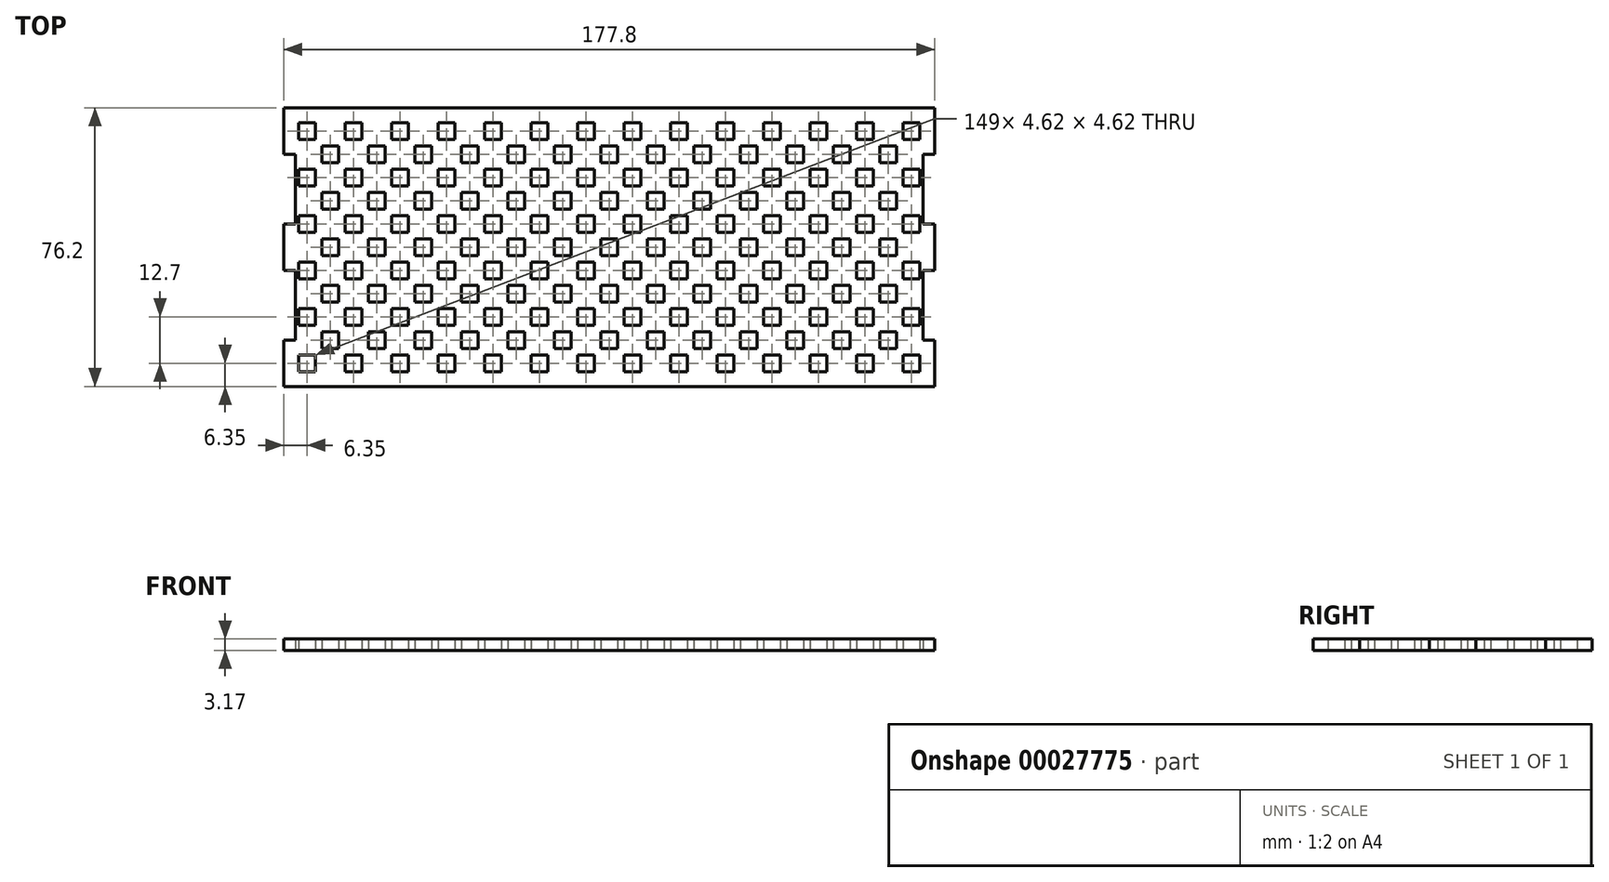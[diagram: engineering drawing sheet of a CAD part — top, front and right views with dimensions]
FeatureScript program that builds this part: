
annotation { "Feature Type Name" : "Feature", "Feature Type Description" : "" }
export const myFeature = defineFeature(function(context is Context, id is Id, definition is map)
    precondition{}
    {
        {
            var Q0;
            Q0=qCreatedBy(makeId("Top.planeOp"),FACE);
            var sketch = newSketch(context, id + "F0", { "sketchPlane" : qUnion([Q0])});
            skLineSegment(sketch, "E0.rect.bottom", {"start": v(88.9, 38.1) * mm, "end": v(-88.9, 38.1) * mm});
            skLineSegment(sketch, "E0.rect.top", {"start": v(88.9, -38.1) * mm, "end": v(-88.9, -38.1) * mm});
            skLineSegment(sketch, "E0.rect.left", {"start": v(88.9, 38.1) * mm, "end": v(88.9, 25.4) * mm});
            skLineSegment(sketch, "E0.rect.right", {"start": v(-88.9, 38.1) * mm, "end": v(-88.9, 25.4) * mm});
            skPoint(sketch, "E0.rect.middle", {"position": v(0, 0) * mm});
            skPoint(sketch, "E1", {"position": v(-88.9, 34.06) * mm});
            skPoint(sketch, "E2", {"position": v(-84.86, 34.06) * mm});
            skLineSegment(sketch, "E3.bottom", {"start": v(-84.86, 34.06) * mm, "end": v(-80.24, 34.06) * mm});
            skLineSegment(sketch, "E3.top", {"start": v(-84.86, 29.44) * mm, "end": v(-80.24, 29.44) * mm});
            skLineSegment(sketch, "E3.left", {"start": v(-84.86, 34.06) * mm, "end": v(-84.86, 29.44) * mm});
            skLineSegment(sketch, "E3.right", {"start": v(-80.24, 34.06) * mm, "end": v(-80.24, 29.44) * mm});
            skLineSegment(sketch, "E4.1.0.0", {"start": v(-72.16, 34.06) * mm, "end": v(-72.16, 29.44) * mm});
            skLineSegment(sketch, "E4.1.0.1", {"start": v(-72.16, 34.06) * mm, "end": v(-67.54, 34.06) * mm});
            skLineSegment(sketch, "E4.1.0.2", {"start": v(-67.54, 34.06) * mm, "end": v(-67.54, 29.44) * mm});
            skLineSegment(sketch, "E4.1.0.3", {"start": v(-72.16, 29.44) * mm, "end": v(-67.54, 29.44) * mm});
            skLineSegment(sketch, "E4.2.0.0", {"start": v(-59.46, 34.06) * mm, "end": v(-59.46, 29.44) * mm});
            skLineSegment(sketch, "E4.2.0.1", {"start": v(-59.46, 34.06) * mm, "end": v(-54.84, 34.06) * mm});
            skLineSegment(sketch, "E4.2.0.2", {"start": v(-54.84, 34.06) * mm, "end": v(-54.84, 29.44) * mm});
            skLineSegment(sketch, "E4.2.0.3", {"start": v(-59.46, 29.44) * mm, "end": v(-54.84, 29.44) * mm});
            skLineSegment(sketch, "E4.3.0.0", {"start": v(-46.76, 34.06) * mm, "end": v(-46.76, 29.44) * mm});
            skLineSegment(sketch, "E4.3.0.1", {"start": v(-46.76, 34.06) * mm, "end": v(-42.14, 34.06) * mm});
            skLineSegment(sketch, "E4.3.0.2", {"start": v(-42.14, 34.06) * mm, "end": v(-42.14, 29.44) * mm});
            skLineSegment(sketch, "E4.3.0.3", {"start": v(-46.76, 29.44) * mm, "end": v(-42.14, 29.44) * mm});
            skLineSegment(sketch, "E4.4.0.0", {"start": v(-34.06, 34.06) * mm, "end": v(-34.06, 29.44) * mm});
            skLineSegment(sketch, "E4.4.0.1", {"start": v(-34.06, 34.06) * mm, "end": v(-29.44, 34.06) * mm});
            skLineSegment(sketch, "E4.4.0.2", {"start": v(-29.44, 34.06) * mm, "end": v(-29.44, 29.44) * mm});
            skLineSegment(sketch, "E4.4.0.3", {"start": v(-34.06, 29.44) * mm, "end": v(-29.44, 29.44) * mm});
            skLineSegment(sketch, "E4.5.0.0", {"start": v(-21.36, 34.06) * mm, "end": v(-21.36, 29.44) * mm});
            skLineSegment(sketch, "E4.5.0.1", {"start": v(-21.36, 34.06) * mm, "end": v(-16.74, 34.06) * mm});
            skLineSegment(sketch, "E4.5.0.2", {"start": v(-16.74, 34.06) * mm, "end": v(-16.74, 29.44) * mm});
            skLineSegment(sketch, "E4.5.0.3", {"start": v(-21.36, 29.44) * mm, "end": v(-16.74, 29.44) * mm});
            skLineSegment(sketch, "E4.6.0.0", {"start": v(-8.66, 34.06) * mm, "end": v(-8.66, 29.44) * mm});
            skLineSegment(sketch, "E4.6.0.1", {"start": v(-8.66, 34.06) * mm, "end": v(-4.04, 34.06) * mm});
            skLineSegment(sketch, "E4.6.0.2", {"start": v(-4.04, 34.06) * mm, "end": v(-4.04, 29.44) * mm});
            skLineSegment(sketch, "E4.6.0.3", {"start": v(-8.66, 29.44) * mm, "end": v(-4.04, 29.44) * mm});
            skLineSegment(sketch, "E4.7.0.0", {"start": v(4.04, 34.06) * mm, "end": v(4.04, 29.44) * mm});
            skLineSegment(sketch, "E4.7.0.1", {"start": v(4.04, 34.06) * mm, "end": v(8.66, 34.06) * mm});
            skLineSegment(sketch, "E4.7.0.2", {"start": v(8.66, 34.06) * mm, "end": v(8.66, 29.44) * mm});
            skLineSegment(sketch, "E4.7.0.3", {"start": v(4.04, 29.44) * mm, "end": v(8.66, 29.44) * mm});
            skLineSegment(sketch, "E4.8.0.0", {"start": v(16.74, 34.06) * mm, "end": v(16.74, 29.44) * mm});
            skLineSegment(sketch, "E4.8.0.1", {"start": v(16.74, 34.06) * mm, "end": v(21.36, 34.06) * mm});
            skLineSegment(sketch, "E4.8.0.2", {"start": v(21.36, 34.06) * mm, "end": v(21.36, 29.44) * mm});
            skLineSegment(sketch, "E4.8.0.3", {"start": v(16.74, 29.44) * mm, "end": v(21.36, 29.44) * mm});
            skLineSegment(sketch, "E4.9.0.0", {"start": v(29.44, 34.06) * mm, "end": v(29.44, 29.44) * mm});
            skLineSegment(sketch, "E4.9.0.1", {"start": v(29.44, 34.06) * mm, "end": v(34.06, 34.06) * mm});
            skLineSegment(sketch, "E4.9.0.2", {"start": v(34.06, 34.06) * mm, "end": v(34.06, 29.44) * mm});
            skLineSegment(sketch, "E4.9.0.3", {"start": v(29.44, 29.44) * mm, "end": v(34.06, 29.44) * mm});
            skLineSegment(sketch, "E4.10.0.0", {"start": v(42.14, 34.06) * mm, "end": v(42.14, 29.44) * mm});
            skLineSegment(sketch, "E4.10.0.1", {"start": v(42.14, 34.06) * mm, "end": v(46.76, 34.06) * mm});
            skLineSegment(sketch, "E4.10.0.2", {"start": v(46.76, 34.06) * mm, "end": v(46.76, 29.44) * mm});
            skLineSegment(sketch, "E4.10.0.3", {"start": v(42.14, 29.44) * mm, "end": v(46.76, 29.44) * mm});
            skLineSegment(sketch, "E4.11.0.0", {"start": v(54.84, 34.06) * mm, "end": v(54.84, 29.44) * mm});
            skLineSegment(sketch, "E4.11.0.1", {"start": v(54.84, 34.06) * mm, "end": v(59.46, 34.06) * mm});
            skLineSegment(sketch, "E4.11.0.2", {"start": v(59.46, 34.06) * mm, "end": v(59.46, 29.44) * mm});
            skLineSegment(sketch, "E4.11.0.3", {"start": v(54.84, 29.44) * mm, "end": v(59.46, 29.44) * mm});
            skLineSegment(sketch, "E4.12.0.0", {"start": v(67.54, 34.06) * mm, "end": v(67.54, 29.44) * mm});
            skLineSegment(sketch, "E4.12.0.1", {"start": v(67.54, 34.06) * mm, "end": v(72.16, 34.06) * mm});
            skLineSegment(sketch, "E4.12.0.2", {"start": v(72.16, 34.06) * mm, "end": v(72.16, 29.44) * mm});
            skLineSegment(sketch, "E4.12.0.3", {"start": v(67.54, 29.44) * mm, "end": v(72.16, 29.44) * mm});
            skLineSegment(sketch, "E4.13.0.0", {"start": v(80.24, 34.06) * mm, "end": v(80.24, 29.44) * mm});
            skLineSegment(sketch, "E4.13.0.1", {"start": v(80.24, 34.06) * mm, "end": v(84.86, 34.06) * mm});
            skLineSegment(sketch, "E4.13.0.2", {"start": v(84.86, 34.06) * mm, "end": v(84.86, 29.44) * mm});
            skLineSegment(sketch, "E4.13.0.3", {"start": v(80.24, 29.44) * mm, "end": v(84.86, 29.44) * mm});
            skLineSegment(sketch, "E4.direction1", {"start": v(-84.86, 29.44) * mm, "end": v(-72.16, 29.44) * mm, "construction": true});
            skPoint(sketch, "E5", {"position": v(88.9, 25.4) * mm});
            skPoint(sketch, "E6", {"position": v(88.9, 6.35) * mm});
            skPoint(sketch, "E7", {"position": v(88.9, -6.35) * mm});
            skPoint(sketch, "E8", {"position": v(88.9, -25.4) * mm});
            skLineSegment(sketch, "E9", {"start": v(88.9, 25.4) * mm, "end": v(85.73, 25.4) * mm});
            skLineSegment(sketch, "E10", {"start": v(85.73, 25.4) * mm, "end": v(85.73, 6.35) * mm});
            skLineSegment(sketch, "E11", {"start": v(85.73, 6.35) * mm, "end": v(88.9, 6.35) * mm});
            skLineSegment(sketch, "E12", {"start": v(88.9, -6.35) * mm, "end": v(85.73, -6.35) * mm});
            skLineSegment(sketch, "E13", {"start": v(85.73, -6.35) * mm, "end": v(85.73, -25.4) * mm});
            skLineSegment(sketch, "E14", {"start": v(85.73, -25.4) * mm, "end": v(88.9, -25.4) * mm});
            skLineSegment(sketch, "E15.trimOffspring", {"start": v(88.9, 6.35) * mm, "end": v(88.9, -6.35) * mm});
            skLineSegment(sketch, "E16.trimOffspring", {"start": v(88.9, -25.4) * mm, "end": v(88.9, -38.1) * mm});
            skLineSegment(sketch, "E17.MirrorCS", {"start": v(-85.73, 25.4) * mm, "end": v(-85.73, 6.35) * mm});
            skLineSegment(sketch, "E18.MirrorCS", {"start": v(-85.73, -6.35) * mm, "end": v(-85.73, -25.4) * mm});
            skLineSegment(sketch, "E19.MirrorCS", {"start": v(-88.9, -6.35) * mm, "end": v(-85.73, -6.35) * mm});
            skLineSegment(sketch, "E20.MirrorCS", {"start": v(-85.73, -25.4) * mm, "end": v(-88.9, -25.4) * mm});
            skLineSegment(sketch, "E21.MirrorCS", {"start": v(-85.73, 6.35) * mm, "end": v(-88.9, 6.35) * mm});
            skLineSegment(sketch, "E22.MirrorCS", {"start": v(-88.9, 25.4) * mm, "end": v(-85.73, 25.4) * mm});
            skLineSegment(sketch, "E23.trimOffspring", {"start": v(-88.9, 6.35) * mm, "end": v(-88.9, -4.04) * mm});
            skLineSegment(sketch, "E24.0.1.35", {"start": v(-84.86, 16.74) * mm, "end": v(-72.16, 16.74) * mm, "construction": true});
            skPoint(sketch, "E24.0.1.36", {"position": v(88.9, 12.7) * mm});
            skPoint(sketch, "E24.0.1.50", {"position": v(-84.86, 21.36) * mm});
            skPoint(sketch, "E24.0.1.57", {"position": v(-88.9, 21.36) * mm});
            skLineSegment(sketch, "E24.0.1.115", {"start": v(-46.76, 21.36) * mm, "end": v(-42.14, 21.36) * mm});
            skLineSegment(sketch, "E24.0.1.116", {"start": v(54.84, 21.36) * mm, "end": v(59.46, 21.36) * mm});
            skLineSegment(sketch, "E24.0.1.117", {"start": v(4.04, 21.36) * mm, "end": v(8.66, 21.36) * mm});
            skLineSegment(sketch, "E24.0.1.118", {"start": v(4.04, 21.36) * mm, "end": v(4.04, 16.74) * mm});
            skLineSegment(sketch, "E24.0.1.119", {"start": v(-21.36, 21.36) * mm, "end": v(-21.36, 16.74) * mm});
            skLineSegment(sketch, "E24.0.1.120", {"start": v(29.44, 21.36) * mm, "end": v(29.44, 16.74) * mm});
            skLineSegment(sketch, "E24.0.1.121", {"start": v(80.24, 21.36) * mm, "end": v(80.24, 16.74) * mm});
            skLineSegment(sketch, "E24.0.1.122", {"start": v(54.84, 21.36) * mm, "end": v(54.84, 16.74) * mm});
            skLineSegment(sketch, "E24.0.1.123", {"start": v(-46.76, 21.36) * mm, "end": v(-46.76, 16.74) * mm});
            skLineSegment(sketch, "E24.0.1.124", {"start": v(-34.06, 16.74) * mm, "end": v(-29.44, 16.74) * mm});
            skLineSegment(sketch, "E24.0.1.125", {"start": v(16.74, 16.74) * mm, "end": v(21.36, 16.74) * mm});
            skLineSegment(sketch, "E24.0.1.126", {"start": v(67.54, 16.74) * mm, "end": v(72.16, 16.74) * mm});
            skLineSegment(sketch, "E24.0.1.127", {"start": v(-59.46, 21.36) * mm, "end": v(-59.46, 16.74) * mm});
            skLineSegment(sketch, "E24.0.1.128", {"start": v(-72.16, 16.74) * mm, "end": v(-67.54, 16.74) * mm});
            skLineSegment(sketch, "E24.0.1.129", {"start": v(-67.54, 21.36) * mm, "end": v(-67.54, 16.74) * mm});
            skLineSegment(sketch, "E24.0.1.130", {"start": v(-72.16, 21.36) * mm, "end": v(-67.54, 21.36) * mm});
            skLineSegment(sketch, "E24.0.1.132", {"start": v(-72.16, 21.36) * mm, "end": v(-72.16, 16.74) * mm});
            skLineSegment(sketch, "E24.0.1.133", {"start": v(-80.24, 21.36) * mm, "end": v(-80.24, 16.74) * mm});
            skLineSegment(sketch, "E24.0.1.134", {"start": v(-84.86, 16.74) * mm, "end": v(-80.24, 16.74) * mm});
            skLineSegment(sketch, "E24.0.1.135", {"start": v(-84.86, 21.36) * mm, "end": v(-80.24, 21.36) * mm});
            skLineSegment(sketch, "E24.0.1.136", {"start": v(-42.14, 21.36) * mm, "end": v(-42.14, 16.74) * mm});
            skLineSegment(sketch, "E24.0.1.137", {"start": v(-59.46, 16.74) * mm, "end": v(-54.84, 16.74) * mm});
            skLineSegment(sketch, "E24.0.1.139", {"start": v(-54.84, 21.36) * mm, "end": v(-54.84, 16.74) * mm});
            skLineSegment(sketch, "E24.0.1.140", {"start": v(-59.46, 21.36) * mm, "end": v(-54.84, 21.36) * mm});
            skLineSegment(sketch, "E24.0.1.141", {"start": v(21.36, 21.36) * mm, "end": v(21.36, 16.74) * mm});
            skLineSegment(sketch, "E24.0.1.142", {"start": v(-8.66, 16.74) * mm, "end": v(-4.04, 16.74) * mm});
            skLineSegment(sketch, "E24.0.1.143", {"start": v(72.16, 21.36) * mm, "end": v(72.16, 16.74) * mm});
            skLineSegment(sketch, "E24.0.1.144", {"start": v(42.14, 16.74) * mm, "end": v(46.76, 16.74) * mm});
            skLineSegment(sketch, "E24.0.1.145", {"start": v(-29.44, 21.36) * mm, "end": v(-29.44, 16.74) * mm});
            skLineSegment(sketch, "E24.0.1.146", {"start": v(54.84, 16.74) * mm, "end": v(59.46, 16.74) * mm});
            skLineSegment(sketch, "E24.0.1.148", {"start": v(-4.04, 21.36) * mm, "end": v(-4.04, 16.74) * mm});
            skLineSegment(sketch, "E24.0.1.149", {"start": v(16.74, 21.36) * mm, "end": v(21.36, 21.36) * mm});
            skLineSegment(sketch, "E24.0.1.150", {"start": v(46.76, 21.36) * mm, "end": v(46.76, 16.74) * mm});
            skLineSegment(sketch, "E24.0.1.151", {"start": v(67.54, 21.36) * mm, "end": v(72.16, 21.36) * mm});
            skLineSegment(sketch, "E24.0.1.152", {"start": v(-8.66, 21.36) * mm, "end": v(-8.66, 16.74) * mm});
            skLineSegment(sketch, "E24.0.1.153", {"start": v(-34.06, 21.36) * mm, "end": v(-29.44, 21.36) * mm});
            skLineSegment(sketch, "E24.0.1.154", {"start": v(42.14, 21.36) * mm, "end": v(42.14, 16.74) * mm});
            skLineSegment(sketch, "E24.0.1.155", {"start": v(-8.66, 21.36) * mm, "end": v(-4.04, 21.36) * mm});
            skLineSegment(sketch, "E24.0.1.156", {"start": v(16.74, 21.36) * mm, "end": v(16.74, 16.74) * mm});
            skLineSegment(sketch, "E24.0.1.157", {"start": v(67.54, 21.36) * mm, "end": v(67.54, 16.74) * mm});
            skLineSegment(sketch, "E24.0.1.158", {"start": v(42.14, 21.36) * mm, "end": v(46.76, 21.36) * mm});
            skLineSegment(sketch, "E24.0.1.159", {"start": v(-34.06, 21.36) * mm, "end": v(-34.06, 16.74) * mm});
            skLineSegment(sketch, "E24.0.1.160", {"start": v(29.44, 16.74) * mm, "end": v(34.06, 16.74) * mm});
            skLineSegment(sketch, "E24.0.1.161", {"start": v(-21.36, 16.74) * mm, "end": v(-16.74, 16.74) * mm});
            skLineSegment(sketch, "E24.0.1.162", {"start": v(80.24, 16.74) * mm, "end": v(84.86, 16.74) * mm});
            skLineSegment(sketch, "E24.0.1.163", {"start": v(-21.36, 21.36) * mm, "end": v(-16.74, 21.36) * mm});
            skLineSegment(sketch, "E24.0.1.164", {"start": v(80.24, 21.36) * mm, "end": v(84.86, 21.36) * mm});
            skLineSegment(sketch, "E24.0.1.165", {"start": v(29.44, 21.36) * mm, "end": v(34.06, 21.36) * mm});
            skLineSegment(sketch, "E24.0.1.166", {"start": v(4.04, 16.74) * mm, "end": v(8.66, 16.74) * mm});
            skLineSegment(sketch, "E24.0.1.167", {"start": v(-46.76, 16.74) * mm, "end": v(-42.14, 16.74) * mm});
            skLineSegment(sketch, "E24.0.1.168", {"start": v(59.46, 21.36) * mm, "end": v(59.46, 16.74) * mm});
            skLineSegment(sketch, "E24.0.1.169", {"start": v(-16.74, 21.36) * mm, "end": v(-16.74, 16.74) * mm});
            skLineSegment(sketch, "E24.0.1.170", {"start": v(34.06, 21.36) * mm, "end": v(34.06, 16.74) * mm});
            skLineSegment(sketch, "E24.0.1.171", {"start": v(8.66, 21.36) * mm, "end": v(8.66, 16.74) * mm});
            skLineSegment(sketch, "E24.0.1.172", {"start": v(84.86, 21.36) * mm, "end": v(84.86, 16.74) * mm});
            skLineSegment(sketch, "E24.0.1.173", {"start": v(-84.86, 21.36) * mm, "end": v(-84.86, 16.74) * mm});
            skLineSegment(sketch, "E24.0.2.35", {"start": v(-84.86, 4.04) * mm, "end": v(-72.16, 4.04) * mm, "construction": true});
            skPoint(sketch, "E24.0.2.36", {"position": v(88.9, 0) * mm});
            skPoint(sketch, "E24.0.2.50", {"position": v(-84.86, 8.66) * mm});
            skPoint(sketch, "E24.0.2.57", {"position": v(-88.9, 8.66) * mm});
            skLineSegment(sketch, "E24.0.2.115", {"start": v(-46.76, 8.66) * mm, "end": v(-42.14, 8.66) * mm});
            skLineSegment(sketch, "E24.0.2.116", {"start": v(54.84, 8.66) * mm, "end": v(59.46, 8.66) * mm});
            skLineSegment(sketch, "E24.0.2.117", {"start": v(4.04, 8.66) * mm, "end": v(8.66, 8.66) * mm});
            skLineSegment(sketch, "E24.0.2.118", {"start": v(4.04, 8.66) * mm, "end": v(4.04, 4.04) * mm});
            skLineSegment(sketch, "E24.0.2.119", {"start": v(-21.36, 8.66) * mm, "end": v(-21.36, 4.04) * mm});
            skLineSegment(sketch, "E24.0.2.120", {"start": v(29.44, 8.66) * mm, "end": v(29.44, 4.04) * mm});
            skLineSegment(sketch, "E24.0.2.121", {"start": v(80.24, 8.66) * mm, "end": v(80.24, 4.04) * mm});
            skLineSegment(sketch, "E24.0.2.122", {"start": v(54.84, 8.66) * mm, "end": v(54.84, 4.04) * mm});
            skLineSegment(sketch, "E24.0.2.123", {"start": v(-46.76, 8.66) * mm, "end": v(-46.76, 4.04) * mm});
            skLineSegment(sketch, "E24.0.2.124", {"start": v(-34.06, 4.04) * mm, "end": v(-29.44, 4.04) * mm});
            skLineSegment(sketch, "E24.0.2.125", {"start": v(16.74, 4.04) * mm, "end": v(21.36, 4.04) * mm});
            skLineSegment(sketch, "E24.0.2.126", {"start": v(67.54, 4.04) * mm, "end": v(72.16, 4.04) * mm});
            skLineSegment(sketch, "E24.0.2.127", {"start": v(-59.46, 8.66) * mm, "end": v(-59.46, 4.04) * mm});
            skLineSegment(sketch, "E24.0.2.128", {"start": v(-72.16, 4.04) * mm, "end": v(-67.54, 4.04) * mm});
            skLineSegment(sketch, "E24.0.2.129", {"start": v(-67.54, 8.66) * mm, "end": v(-67.54, 4.04) * mm});
            skLineSegment(sketch, "E24.0.2.130", {"start": v(-72.16, 8.66) * mm, "end": v(-67.54, 8.66) * mm});
            skLineSegment(sketch, "E24.0.2.132", {"start": v(-72.16, 8.66) * mm, "end": v(-72.16, 4.04) * mm});
            skLineSegment(sketch, "E24.0.2.133", {"start": v(-80.24, 8.66) * mm, "end": v(-80.24, 4.04) * mm});
            skLineSegment(sketch, "E24.0.2.134", {"start": v(-84.86, 4.04) * mm, "end": v(-80.24, 4.04) * mm});
            skLineSegment(sketch, "E24.0.2.135", {"start": v(-84.86, 8.66) * mm, "end": v(-80.24, 8.66) * mm});
            skLineSegment(sketch, "E24.0.2.136", {"start": v(-42.14, 8.66) * mm, "end": v(-42.14, 4.04) * mm});
            skLineSegment(sketch, "E24.0.2.137", {"start": v(-59.46, 4.04) * mm, "end": v(-54.84, 4.04) * mm});
            skLineSegment(sketch, "E24.0.2.139", {"start": v(-54.84, 8.66) * mm, "end": v(-54.84, 4.04) * mm});
            skLineSegment(sketch, "E24.0.2.140", {"start": v(-59.46, 8.66) * mm, "end": v(-54.84, 8.66) * mm});
            skLineSegment(sketch, "E24.0.2.141", {"start": v(21.36, 8.66) * mm, "end": v(21.36, 4.04) * mm});
            skLineSegment(sketch, "E24.0.2.142", {"start": v(-8.66, 4.04) * mm, "end": v(-4.04, 4.04) * mm});
            skLineSegment(sketch, "E24.0.2.143", {"start": v(72.16, 8.66) * mm, "end": v(72.16, 4.04) * mm});
            skLineSegment(sketch, "E24.0.2.144", {"start": v(42.14, 4.04) * mm, "end": v(46.76, 4.04) * mm});
            skLineSegment(sketch, "E24.0.2.145", {"start": v(-29.44, 8.66) * mm, "end": v(-29.44, 4.04) * mm});
            skLineSegment(sketch, "E24.0.2.146", {"start": v(54.84, 4.04) * mm, "end": v(59.46, 4.04) * mm});
            skLineSegment(sketch, "E24.0.2.148", {"start": v(-4.04, 8.66) * mm, "end": v(-4.04, 4.04) * mm});
            skLineSegment(sketch, "E24.0.2.149", {"start": v(16.74, 8.66) * mm, "end": v(21.36, 8.66) * mm});
            skLineSegment(sketch, "E24.0.2.150", {"start": v(46.76, 8.66) * mm, "end": v(46.76, 4.04) * mm});
            skLineSegment(sketch, "E24.0.2.151", {"start": v(67.54, 8.66) * mm, "end": v(72.16, 8.66) * mm});
            skLineSegment(sketch, "E24.0.2.152", {"start": v(-8.66, 8.66) * mm, "end": v(-8.66, 4.04) * mm});
            skLineSegment(sketch, "E24.0.2.153", {"start": v(-34.06, 8.66) * mm, "end": v(-29.44, 8.66) * mm});
            skLineSegment(sketch, "E24.0.2.154", {"start": v(42.14, 8.66) * mm, "end": v(42.14, 4.04) * mm});
            skLineSegment(sketch, "E24.0.2.155", {"start": v(-8.66, 8.66) * mm, "end": v(-4.04, 8.66) * mm});
            skLineSegment(sketch, "E24.0.2.156", {"start": v(16.74, 8.66) * mm, "end": v(16.74, 4.04) * mm});
            skLineSegment(sketch, "E24.0.2.157", {"start": v(67.54, 8.66) * mm, "end": v(67.54, 4.04) * mm});
            skLineSegment(sketch, "E24.0.2.158", {"start": v(42.14, 8.66) * mm, "end": v(46.76, 8.66) * mm});
            skLineSegment(sketch, "E24.0.2.159", {"start": v(-34.06, 8.66) * mm, "end": v(-34.06, 4.04) * mm});
            skLineSegment(sketch, "E24.0.2.160", {"start": v(29.44, 4.04) * mm, "end": v(34.06, 4.04) * mm});
            skLineSegment(sketch, "E24.0.2.161", {"start": v(-21.36, 4.04) * mm, "end": v(-16.74, 4.04) * mm});
            skLineSegment(sketch, "E24.0.2.162", {"start": v(80.24, 4.04) * mm, "end": v(84.86, 4.04) * mm});
            skLineSegment(sketch, "E24.0.2.163", {"start": v(-21.36, 8.66) * mm, "end": v(-16.74, 8.66) * mm});
            skLineSegment(sketch, "E24.0.2.164", {"start": v(80.24, 8.66) * mm, "end": v(84.86, 8.66) * mm});
            skLineSegment(sketch, "E24.0.2.165", {"start": v(29.44, 8.66) * mm, "end": v(34.06, 8.66) * mm});
            skLineSegment(sketch, "E24.0.2.166", {"start": v(4.04, 4.04) * mm, "end": v(8.66, 4.04) * mm});
            skLineSegment(sketch, "E24.0.2.167", {"start": v(-46.76, 4.04) * mm, "end": v(-42.14, 4.04) * mm});
            skLineSegment(sketch, "E24.0.2.168", {"start": v(59.46, 8.66) * mm, "end": v(59.46, 4.04) * mm});
            skLineSegment(sketch, "E24.0.2.169", {"start": v(-16.74, 8.66) * mm, "end": v(-16.74, 4.04) * mm});
            skLineSegment(sketch, "E24.0.2.170", {"start": v(34.06, 8.66) * mm, "end": v(34.06, 4.04) * mm});
            skLineSegment(sketch, "E24.0.2.171", {"start": v(8.66, 8.66) * mm, "end": v(8.66, 4.04) * mm});
            skLineSegment(sketch, "E24.0.2.172", {"start": v(84.86, 8.66) * mm, "end": v(84.86, 4.04) * mm});
            skLineSegment(sketch, "E24.0.2.173", {"start": v(-84.86, 8.66) * mm, "end": v(-84.86, 4.04) * mm});
            skLineSegment(sketch, "E24.0.3.35", {"start": v(-84.86, -8.66) * mm, "end": v(-72.16, -8.66) * mm, "construction": true});
            skPoint(sketch, "E24.0.3.36", {"position": v(88.9, -12.7) * mm});
            skPoint(sketch, "E24.0.3.50", {"position": v(-84.86, -4.04) * mm});
            skPoint(sketch, "E24.0.3.57", {"position": v(-88.9, -4.04) * mm});
            skLineSegment(sketch, "E24.0.3.115", {"start": v(-46.76, -4.04) * mm, "end": v(-42.14, -4.04) * mm});
            skLineSegment(sketch, "E24.0.3.116", {"start": v(54.84, -4.04) * mm, "end": v(59.46, -4.04) * mm});
            skLineSegment(sketch, "E24.0.3.117", {"start": v(4.04, -4.04) * mm, "end": v(8.66, -4.04) * mm});
            skLineSegment(sketch, "E24.0.3.118", {"start": v(4.04, -4.04) * mm, "end": v(4.04, -8.66) * mm});
            skLineSegment(sketch, "E24.0.3.119", {"start": v(-21.36, -4.04) * mm, "end": v(-21.36, -8.66) * mm});
            skLineSegment(sketch, "E24.0.3.120", {"start": v(29.44, -4.04) * mm, "end": v(29.44, -8.66) * mm});
            skLineSegment(sketch, "E24.0.3.121", {"start": v(80.24, -4.04) * mm, "end": v(80.24, -8.66) * mm});
            skLineSegment(sketch, "E24.0.3.122", {"start": v(54.84, -4.04) * mm, "end": v(54.84, -8.66) * mm});
            skLineSegment(sketch, "E24.0.3.123", {"start": v(-46.76, -4.04) * mm, "end": v(-46.76, -8.66) * mm});
            skLineSegment(sketch, "E24.0.3.124", {"start": v(-34.06, -8.66) * mm, "end": v(-29.44, -8.66) * mm});
            skLineSegment(sketch, "E24.0.3.125", {"start": v(16.74, -8.66) * mm, "end": v(21.36, -8.66) * mm});
            skLineSegment(sketch, "E24.0.3.126", {"start": v(67.54, -8.66) * mm, "end": v(72.16, -8.66) * mm});
            skLineSegment(sketch, "E24.0.3.127", {"start": v(-59.46, -4.04) * mm, "end": v(-59.46, -8.66) * mm});
            skLineSegment(sketch, "E24.0.3.128", {"start": v(-72.16, -8.66) * mm, "end": v(-67.54, -8.66) * mm});
            skLineSegment(sketch, "E24.0.3.129", {"start": v(-67.54, -4.04) * mm, "end": v(-67.54, -8.66) * mm});
            skLineSegment(sketch, "E24.0.3.130", {"start": v(-72.16, -4.04) * mm, "end": v(-67.54, -4.04) * mm});
            skLineSegment(sketch, "E24.0.3.132", {"start": v(-72.16, -4.04) * mm, "end": v(-72.16, -8.66) * mm});
            skLineSegment(sketch, "E24.0.3.133", {"start": v(-80.24, -4.04) * mm, "end": v(-80.24, -8.66) * mm});
            skLineSegment(sketch, "E24.0.3.134", {"start": v(-84.86, -8.66) * mm, "end": v(-80.24, -8.66) * mm});
            skLineSegment(sketch, "E24.0.3.135", {"start": v(-84.86, -4.04) * mm, "end": v(-80.24, -4.04) * mm});
            skLineSegment(sketch, "E24.0.3.136", {"start": v(-42.14, -4.04) * mm, "end": v(-42.14, -8.66) * mm});
            skLineSegment(sketch, "E24.0.3.137", {"start": v(-59.46, -8.66) * mm, "end": v(-54.84, -8.66) * mm});
            skLineSegment(sketch, "E24.0.3.139", {"start": v(-54.84, -4.04) * mm, "end": v(-54.84, -8.66) * mm});
            skLineSegment(sketch, "E24.0.3.140", {"start": v(-59.46, -4.04) * mm, "end": v(-54.84, -4.04) * mm});
            skLineSegment(sketch, "E24.0.3.141", {"start": v(21.36, -4.04) * mm, "end": v(21.36, -8.66) * mm});
            skLineSegment(sketch, "E24.0.3.142", {"start": v(-8.66, -8.66) * mm, "end": v(-4.04, -8.66) * mm});
            skLineSegment(sketch, "E24.0.3.143", {"start": v(72.16, -4.04) * mm, "end": v(72.16, -8.66) * mm});
            skLineSegment(sketch, "E24.0.3.144", {"start": v(42.14, -8.66) * mm, "end": v(46.76, -8.66) * mm});
            skLineSegment(sketch, "E24.0.3.145", {"start": v(-29.44, -4.04) * mm, "end": v(-29.44, -8.66) * mm});
            skLineSegment(sketch, "E24.0.3.146", {"start": v(54.84, -8.66) * mm, "end": v(59.46, -8.66) * mm});
            skLineSegment(sketch, "E24.0.3.148", {"start": v(-4.04, -4.04) * mm, "end": v(-4.04, -8.66) * mm});
            skLineSegment(sketch, "E24.0.3.149", {"start": v(16.74, -4.04) * mm, "end": v(21.36, -4.04) * mm});
            skLineSegment(sketch, "E24.0.3.150", {"start": v(46.76, -4.04) * mm, "end": v(46.76, -8.66) * mm});
            skLineSegment(sketch, "E24.0.3.151", {"start": v(67.54, -4.04) * mm, "end": v(72.16, -4.04) * mm});
            skLineSegment(sketch, "E24.0.3.152", {"start": v(-8.66, -4.04) * mm, "end": v(-8.66, -8.66) * mm});
            skLineSegment(sketch, "E24.0.3.153", {"start": v(-34.06, -4.04) * mm, "end": v(-29.44, -4.04) * mm});
            skLineSegment(sketch, "E24.0.3.154", {"start": v(42.14, -4.04) * mm, "end": v(42.14, -8.66) * mm});
            skLineSegment(sketch, "E24.0.3.155", {"start": v(-8.66, -4.04) * mm, "end": v(-4.04, -4.04) * mm});
            skLineSegment(sketch, "E24.0.3.156", {"start": v(16.74, -4.04) * mm, "end": v(16.74, -8.66) * mm});
            skLineSegment(sketch, "E24.0.3.157", {"start": v(67.54, -4.04) * mm, "end": v(67.54, -8.66) * mm});
            skLineSegment(sketch, "E24.0.3.158", {"start": v(42.14, -4.04) * mm, "end": v(46.76, -4.04) * mm});
            skLineSegment(sketch, "E24.0.3.159", {"start": v(-34.06, -4.04) * mm, "end": v(-34.06, -8.66) * mm});
            skLineSegment(sketch, "E24.0.3.160", {"start": v(29.44, -8.66) * mm, "end": v(34.06, -8.66) * mm});
            skLineSegment(sketch, "E24.0.3.161", {"start": v(-21.36, -8.66) * mm, "end": v(-16.74, -8.66) * mm});
            skLineSegment(sketch, "E24.0.3.162", {"start": v(80.24, -8.66) * mm, "end": v(84.86, -8.66) * mm});
            skLineSegment(sketch, "E24.0.3.163", {"start": v(-21.36, -4.04) * mm, "end": v(-16.74, -4.04) * mm});
            skLineSegment(sketch, "E24.0.3.164", {"start": v(80.24, -4.04) * mm, "end": v(84.86, -4.04) * mm});
            skLineSegment(sketch, "E24.0.3.165", {"start": v(29.44, -4.04) * mm, "end": v(34.06, -4.04) * mm});
            skLineSegment(sketch, "E24.0.3.166", {"start": v(4.04, -8.66) * mm, "end": v(8.66, -8.66) * mm});
            skLineSegment(sketch, "E24.0.3.167", {"start": v(-46.76, -8.66) * mm, "end": v(-42.14, -8.66) * mm});
            skLineSegment(sketch, "E24.0.3.168", {"start": v(59.46, -4.04) * mm, "end": v(59.46, -8.66) * mm});
            skLineSegment(sketch, "E24.0.3.169", {"start": v(-16.74, -4.04) * mm, "end": v(-16.74, -8.66) * mm});
            skLineSegment(sketch, "E24.0.3.170", {"start": v(34.06, -4.04) * mm, "end": v(34.06, -8.66) * mm});
            skLineSegment(sketch, "E24.0.3.171", {"start": v(8.66, -4.04) * mm, "end": v(8.66, -8.66) * mm});
            skLineSegment(sketch, "E24.0.3.172", {"start": v(84.86, -4.04) * mm, "end": v(84.86, -8.66) * mm});
            skLineSegment(sketch, "E24.0.3.173", {"start": v(-84.86, -4.04) * mm, "end": v(-84.86, -8.66) * mm});
            skLineSegment(sketch, "E24.0.4.35", {"start": v(-84.86, -21.36) * mm, "end": v(-72.16, -21.36) * mm, "construction": true});
            skPoint(sketch, "E24.0.4.50", {"position": v(-84.86, -16.74) * mm});
            skPoint(sketch, "E24.0.4.57", {"position": v(-88.9, -16.74) * mm});
            skLineSegment(sketch, "E24.0.4.115", {"start": v(-46.76, -16.74) * mm, "end": v(-42.14, -16.74) * mm});
            skLineSegment(sketch, "E24.0.4.116", {"start": v(54.84, -16.74) * mm, "end": v(59.46, -16.74) * mm});
            skLineSegment(sketch, "E24.0.4.117", {"start": v(4.04, -16.74) * mm, "end": v(8.66, -16.74) * mm});
            skLineSegment(sketch, "E24.0.4.118", {"start": v(4.04, -16.74) * mm, "end": v(4.04, -21.36) * mm});
            skLineSegment(sketch, "E24.0.4.119", {"start": v(-21.36, -16.74) * mm, "end": v(-21.36, -21.36) * mm});
            skLineSegment(sketch, "E24.0.4.120", {"start": v(29.44, -16.74) * mm, "end": v(29.44, -21.36) * mm});
            skLineSegment(sketch, "E24.0.4.121", {"start": v(80.24, -16.74) * mm, "end": v(80.24, -21.36) * mm});
            skLineSegment(sketch, "E24.0.4.122", {"start": v(54.84, -16.74) * mm, "end": v(54.84, -21.36) * mm});
            skLineSegment(sketch, "E24.0.4.123", {"start": v(-46.76, -16.74) * mm, "end": v(-46.76, -21.36) * mm});
            skLineSegment(sketch, "E24.0.4.124", {"start": v(-34.06, -21.36) * mm, "end": v(-29.44, -21.36) * mm});
            skLineSegment(sketch, "E24.0.4.125", {"start": v(16.74, -21.36) * mm, "end": v(21.36, -21.36) * mm});
            skLineSegment(sketch, "E24.0.4.126", {"start": v(67.54, -21.36) * mm, "end": v(72.16, -21.36) * mm});
            skLineSegment(sketch, "E24.0.4.127", {"start": v(-59.46, -16.74) * mm, "end": v(-59.46, -21.36) * mm});
            skLineSegment(sketch, "E24.0.4.128", {"start": v(-72.16, -21.36) * mm, "end": v(-67.54, -21.36) * mm});
            skLineSegment(sketch, "E24.0.4.129", {"start": v(-67.54, -16.74) * mm, "end": v(-67.54, -21.36) * mm});
            skLineSegment(sketch, "E24.0.4.130", {"start": v(-72.16, -16.74) * mm, "end": v(-67.54, -16.74) * mm});
            skLineSegment(sketch, "E24.0.4.132", {"start": v(-72.16, -16.74) * mm, "end": v(-72.16, -21.36) * mm});
            skLineSegment(sketch, "E24.0.4.133", {"start": v(-80.24, -16.74) * mm, "end": v(-80.24, -21.36) * mm});
            skLineSegment(sketch, "E24.0.4.134", {"start": v(-84.86, -21.36) * mm, "end": v(-80.24, -21.36) * mm});
            skLineSegment(sketch, "E24.0.4.135", {"start": v(-84.86, -16.74) * mm, "end": v(-80.24, -16.74) * mm});
            skLineSegment(sketch, "E24.0.4.136", {"start": v(-42.14, -16.74) * mm, "end": v(-42.14, -21.36) * mm});
            skLineSegment(sketch, "E24.0.4.137", {"start": v(-59.46, -21.36) * mm, "end": v(-54.84, -21.36) * mm});
            skLineSegment(sketch, "E24.0.4.139", {"start": v(-54.84, -16.74) * mm, "end": v(-54.84, -21.36) * mm});
            skLineSegment(sketch, "E24.0.4.140", {"start": v(-59.46, -16.74) * mm, "end": v(-54.84, -16.74) * mm});
            skLineSegment(sketch, "E24.0.4.141", {"start": v(21.36, -16.74) * mm, "end": v(21.36, -21.36) * mm});
            skLineSegment(sketch, "E24.0.4.142", {"start": v(-8.66, -21.36) * mm, "end": v(-4.04, -21.36) * mm});
            skLineSegment(sketch, "E24.0.4.143", {"start": v(72.16, -16.74) * mm, "end": v(72.16, -21.36) * mm});
            skLineSegment(sketch, "E24.0.4.144", {"start": v(42.14, -21.36) * mm, "end": v(46.76, -21.36) * mm});
            skLineSegment(sketch, "E24.0.4.145", {"start": v(-29.44, -16.74) * mm, "end": v(-29.44, -21.36) * mm});
            skLineSegment(sketch, "E24.0.4.146", {"start": v(54.84, -21.36) * mm, "end": v(59.46, -21.36) * mm});
            skLineSegment(sketch, "E24.0.4.148", {"start": v(-4.04, -16.74) * mm, "end": v(-4.04, -21.36) * mm});
            skLineSegment(sketch, "E24.0.4.149", {"start": v(16.74, -16.74) * mm, "end": v(21.36, -16.74) * mm});
            skLineSegment(sketch, "E24.0.4.150", {"start": v(46.76, -16.74) * mm, "end": v(46.76, -21.36) * mm});
            skLineSegment(sketch, "E24.0.4.151", {"start": v(67.54, -16.74) * mm, "end": v(72.16, -16.74) * mm});
            skLineSegment(sketch, "E24.0.4.152", {"start": v(-8.66, -16.74) * mm, "end": v(-8.66, -21.36) * mm});
            skLineSegment(sketch, "E24.0.4.153", {"start": v(-34.06, -16.74) * mm, "end": v(-29.44, -16.74) * mm});
            skLineSegment(sketch, "E24.0.4.154", {"start": v(42.14, -16.74) * mm, "end": v(42.14, -21.36) * mm});
            skLineSegment(sketch, "E24.0.4.155", {"start": v(-8.66, -16.74) * mm, "end": v(-4.04, -16.74) * mm});
            skLineSegment(sketch, "E24.0.4.156", {"start": v(16.74, -16.74) * mm, "end": v(16.74, -21.36) * mm});
            skLineSegment(sketch, "E24.0.4.157", {"start": v(67.54, -16.74) * mm, "end": v(67.54, -21.36) * mm});
            skLineSegment(sketch, "E24.0.4.158", {"start": v(42.14, -16.74) * mm, "end": v(46.76, -16.74) * mm});
            skLineSegment(sketch, "E24.0.4.159", {"start": v(-34.06, -16.74) * mm, "end": v(-34.06, -21.36) * mm});
            skLineSegment(sketch, "E24.0.4.160", {"start": v(29.44, -21.36) * mm, "end": v(34.06, -21.36) * mm});
            skLineSegment(sketch, "E24.0.4.161", {"start": v(-21.36, -21.36) * mm, "end": v(-16.74, -21.36) * mm});
            skLineSegment(sketch, "E24.0.4.162", {"start": v(80.24, -21.36) * mm, "end": v(84.86, -21.36) * mm});
            skLineSegment(sketch, "E24.0.4.163", {"start": v(-21.36, -16.74) * mm, "end": v(-16.74, -16.74) * mm});
            skLineSegment(sketch, "E24.0.4.164", {"start": v(80.24, -16.74) * mm, "end": v(84.86, -16.74) * mm});
            skLineSegment(sketch, "E24.0.4.165", {"start": v(29.44, -16.74) * mm, "end": v(34.06, -16.74) * mm});
            skLineSegment(sketch, "E24.0.4.166", {"start": v(4.04, -21.36) * mm, "end": v(8.66, -21.36) * mm});
            skLineSegment(sketch, "E24.0.4.167", {"start": v(-46.76, -21.36) * mm, "end": v(-42.14, -21.36) * mm});
            skLineSegment(sketch, "E24.0.4.168", {"start": v(59.46, -16.74) * mm, "end": v(59.46, -21.36) * mm});
            skLineSegment(sketch, "E24.0.4.169", {"start": v(-16.74, -16.74) * mm, "end": v(-16.74, -21.36) * mm});
            skLineSegment(sketch, "E24.0.4.170", {"start": v(34.06, -16.74) * mm, "end": v(34.06, -21.36) * mm});
            skLineSegment(sketch, "E24.0.4.171", {"start": v(8.66, -16.74) * mm, "end": v(8.66, -21.36) * mm});
            skLineSegment(sketch, "E24.0.4.172", {"start": v(84.86, -16.74) * mm, "end": v(84.86, -21.36) * mm});
            skLineSegment(sketch, "E24.0.4.173", {"start": v(-84.86, -16.74) * mm, "end": v(-84.86, -21.36) * mm});
            skLineSegment(sketch, "E24.0.5.35", {"start": v(-84.86, -34.06) * mm, "end": v(-72.16, -34.06) * mm, "construction": true});
            skPoint(sketch, "E24.0.5.36", {"position": v(88.9, -38.1) * mm});
            skPoint(sketch, "E24.0.5.50", {"position": v(-84.86, -29.44) * mm});
            skPoint(sketch, "E24.0.5.57", {"position": v(-88.9, -29.44) * mm});
            skLineSegment(sketch, "E24.0.5.115", {"start": v(-46.76, -29.44) * mm, "end": v(-42.14, -29.44) * mm});
            skLineSegment(sketch, "E24.0.5.116", {"start": v(54.84, -29.44) * mm, "end": v(59.46, -29.44) * mm});
            skLineSegment(sketch, "E24.0.5.117", {"start": v(4.04, -29.44) * mm, "end": v(8.66, -29.44) * mm});
            skLineSegment(sketch, "E24.0.5.118", {"start": v(4.04, -29.44) * mm, "end": v(4.04, -34.06) * mm});
            skLineSegment(sketch, "E24.0.5.119", {"start": v(-21.36, -29.44) * mm, "end": v(-21.36, -34.06) * mm});
            skLineSegment(sketch, "E24.0.5.120", {"start": v(29.44, -29.44) * mm, "end": v(29.44, -34.06) * mm});
            skLineSegment(sketch, "E24.0.5.121", {"start": v(80.24, -29.44) * mm, "end": v(80.24, -34.06) * mm});
            skLineSegment(sketch, "E24.0.5.122", {"start": v(54.84, -29.44) * mm, "end": v(54.84, -34.06) * mm});
            skLineSegment(sketch, "E24.0.5.123", {"start": v(-46.76, -29.44) * mm, "end": v(-46.76, -34.06) * mm});
            skLineSegment(sketch, "E24.0.5.124", {"start": v(-34.06, -34.06) * mm, "end": v(-29.44, -34.06) * mm});
            skLineSegment(sketch, "E24.0.5.125", {"start": v(16.74, -34.06) * mm, "end": v(21.36, -34.06) * mm});
            skLineSegment(sketch, "E24.0.5.126", {"start": v(67.54, -34.06) * mm, "end": v(72.16, -34.06) * mm});
            skLineSegment(sketch, "E24.0.5.127", {"start": v(-59.46, -29.44) * mm, "end": v(-59.46, -34.06) * mm});
            skLineSegment(sketch, "E24.0.5.128", {"start": v(-72.16, -34.06) * mm, "end": v(-67.54, -34.06) * mm});
            skLineSegment(sketch, "E24.0.5.129", {"start": v(-67.54, -29.44) * mm, "end": v(-67.54, -34.06) * mm});
            skLineSegment(sketch, "E24.0.5.130", {"start": v(-72.16, -29.44) * mm, "end": v(-67.54, -29.44) * mm});
            skLineSegment(sketch, "E24.0.5.132", {"start": v(-72.16, -29.44) * mm, "end": v(-72.16, -34.06) * mm});
            skLineSegment(sketch, "E24.0.5.133", {"start": v(-80.24, -29.44) * mm, "end": v(-80.24, -34.06) * mm});
            skLineSegment(sketch, "E24.0.5.134", {"start": v(-84.86, -34.06) * mm, "end": v(-80.24, -34.06) * mm});
            skLineSegment(sketch, "E24.0.5.135", {"start": v(-84.86, -29.44) * mm, "end": v(-80.24, -29.44) * mm});
            skLineSegment(sketch, "E24.0.5.136", {"start": v(-42.14, -29.44) * mm, "end": v(-42.14, -34.06) * mm});
            skLineSegment(sketch, "E24.0.5.137", {"start": v(-59.46, -34.06) * mm, "end": v(-54.84, -34.06) * mm});
            skLineSegment(sketch, "E24.0.5.139", {"start": v(-54.84, -29.44) * mm, "end": v(-54.84, -34.06) * mm});
            skLineSegment(sketch, "E24.0.5.140", {"start": v(-59.46, -29.44) * mm, "end": v(-54.84, -29.44) * mm});
            skLineSegment(sketch, "E24.0.5.141", {"start": v(21.36, -29.44) * mm, "end": v(21.36, -34.06) * mm});
            skLineSegment(sketch, "E24.0.5.142", {"start": v(-8.66, -34.06) * mm, "end": v(-4.04, -34.06) * mm});
            skLineSegment(sketch, "E24.0.5.143", {"start": v(72.16, -29.44) * mm, "end": v(72.16, -34.06) * mm});
            skLineSegment(sketch, "E24.0.5.144", {"start": v(42.14, -34.06) * mm, "end": v(46.76, -34.06) * mm});
            skLineSegment(sketch, "E24.0.5.145", {"start": v(-29.44, -29.44) * mm, "end": v(-29.44, -34.06) * mm});
            skLineSegment(sketch, "E24.0.5.146", {"start": v(54.84, -34.06) * mm, "end": v(59.46, -34.06) * mm});
            skLineSegment(sketch, "E24.0.5.148", {"start": v(-4.04, -29.44) * mm, "end": v(-4.04, -34.06) * mm});
            skLineSegment(sketch, "E24.0.5.149", {"start": v(16.74, -29.44) * mm, "end": v(21.36, -29.44) * mm});
            skLineSegment(sketch, "E24.0.5.150", {"start": v(46.76, -29.44) * mm, "end": v(46.76, -34.06) * mm});
            skLineSegment(sketch, "E24.0.5.151", {"start": v(67.54, -29.44) * mm, "end": v(72.16, -29.44) * mm});
            skLineSegment(sketch, "E24.0.5.152", {"start": v(-8.66, -29.44) * mm, "end": v(-8.66, -34.06) * mm});
            skLineSegment(sketch, "E24.0.5.153", {"start": v(-34.06, -29.44) * mm, "end": v(-29.44, -29.44) * mm});
            skLineSegment(sketch, "E24.0.5.154", {"start": v(42.14, -29.44) * mm, "end": v(42.14, -34.06) * mm});
            skLineSegment(sketch, "E24.0.5.155", {"start": v(-8.66, -29.44) * mm, "end": v(-4.04, -29.44) * mm});
            skLineSegment(sketch, "E24.0.5.156", {"start": v(16.74, -29.44) * mm, "end": v(16.74, -34.06) * mm});
            skLineSegment(sketch, "E24.0.5.157", {"start": v(67.54, -29.44) * mm, "end": v(67.54, -34.06) * mm});
            skLineSegment(sketch, "E24.0.5.158", {"start": v(42.14, -29.44) * mm, "end": v(46.76, -29.44) * mm});
            skLineSegment(sketch, "E24.0.5.159", {"start": v(-34.06, -29.44) * mm, "end": v(-34.06, -34.06) * mm});
            skLineSegment(sketch, "E24.0.5.160", {"start": v(29.44, -34.06) * mm, "end": v(34.06, -34.06) * mm});
            skLineSegment(sketch, "E24.0.5.161", {"start": v(-21.36, -34.06) * mm, "end": v(-16.74, -34.06) * mm});
            skLineSegment(sketch, "E24.0.5.162", {"start": v(80.24, -34.06) * mm, "end": v(84.86, -34.06) * mm});
            skLineSegment(sketch, "E24.0.5.163", {"start": v(-21.36, -29.44) * mm, "end": v(-16.74, -29.44) * mm});
            skLineSegment(sketch, "E24.0.5.164", {"start": v(80.24, -29.44) * mm, "end": v(84.86, -29.44) * mm});
            skLineSegment(sketch, "E24.0.5.165", {"start": v(29.44, -29.44) * mm, "end": v(34.06, -29.44) * mm});
            skLineSegment(sketch, "E24.0.5.166", {"start": v(4.04, -34.06) * mm, "end": v(8.66, -34.06) * mm});
            skLineSegment(sketch, "E24.0.5.167", {"start": v(-46.76, -34.06) * mm, "end": v(-42.14, -34.06) * mm});
            skLineSegment(sketch, "E24.0.5.168", {"start": v(59.46, -29.44) * mm, "end": v(59.46, -34.06) * mm});
            skLineSegment(sketch, "E24.0.5.169", {"start": v(-16.74, -29.44) * mm, "end": v(-16.74, -34.06) * mm});
            skLineSegment(sketch, "E24.0.5.170", {"start": v(34.06, -29.44) * mm, "end": v(34.06, -34.06) * mm});
            skLineSegment(sketch, "E24.0.5.171", {"start": v(8.66, -29.44) * mm, "end": v(8.66, -34.06) * mm});
            skLineSegment(sketch, "E24.0.5.172", {"start": v(84.86, -29.44) * mm, "end": v(84.86, -34.06) * mm});
            skLineSegment(sketch, "E24.0.5.173", {"start": v(-84.86, -29.44) * mm, "end": v(-84.86, -34.06) * mm});
            skLineSegment(sketch, "E24.direction1", {"start": v(42.14, 34.06) * mm, "end": v(67.54, 34.06) * mm, "construction": true});
            skLineSegment(sketch, "E24.direction2", {"start": v(42.14, 34.06) * mm, "end": v(42.14, 21.36) * mm, "construction": true});
            skLineSegment(sketch, "E25.trimOffspring", {"start": v(-88.9, -25.4) * mm, "end": v(-88.9, -38.1) * mm});
            skLineSegment(sketch, "E26", {"start": v(-88.9, -6.35) * mm, "end": v(-88.9, -4.04) * mm});
            skLineSegment(sketch, "E27.rect.bottom", {"start": v(-78.51, 23.09) * mm, "end": v(-73.89, 23.09) * mm});
            skLineSegment(sketch, "E27.rect.top", {"start": v(-78.51, 27.71) * mm, "end": v(-73.89, 27.71) * mm});
            skLineSegment(sketch, "E27.rect.left", {"start": v(-78.51, 23.09) * mm, "end": v(-78.51, 27.71) * mm});
            skLineSegment(sketch, "E27.rect.right", {"start": v(-73.89, 23.09) * mm, "end": v(-73.89, 27.71) * mm});
            skPoint(sketch, "E27.rect.middle", {"position": v(-76.2, 25.4) * mm});
            skLineSegment(sketch, "E28.0.1.0", {"start": v(-78.51, 15.01) * mm, "end": v(-73.89, 15.01) * mm});
            skLineSegment(sketch, "E28.0.1.1", {"start": v(-73.89, 10.39) * mm, "end": v(-73.89, 15.01) * mm});
            skLineSegment(sketch, "E28.0.1.2", {"start": v(-78.51, 10.39) * mm, "end": v(-73.89, 10.39) * mm});
            skLineSegment(sketch, "E28.0.1.3", {"start": v(-78.51, 10.39) * mm, "end": v(-78.51, 15.01) * mm});
            skLineSegment(sketch, "E28.0.2.0", {"start": v(-78.51, 2.31) * mm, "end": v(-73.89, 2.31) * mm});
            skLineSegment(sketch, "E28.0.2.1", {"start": v(-73.89, -2.31) * mm, "end": v(-73.89, 2.31) * mm});
            skLineSegment(sketch, "E28.0.2.2", {"start": v(-78.51, -2.31) * mm, "end": v(-73.89, -2.31) * mm});
            skLineSegment(sketch, "E28.0.2.3", {"start": v(-78.51, -2.31) * mm, "end": v(-78.51, 2.31) * mm});
            skLineSegment(sketch, "E28.0.3.0", {"start": v(-78.51, -10.39) * mm, "end": v(-73.89, -10.39) * mm});
            skLineSegment(sketch, "E28.0.3.1", {"start": v(-73.89, -15.01) * mm, "end": v(-73.89, -10.39) * mm});
            skLineSegment(sketch, "E28.0.3.2", {"start": v(-78.51, -15.01) * mm, "end": v(-73.89, -15.01) * mm});
            skLineSegment(sketch, "E28.0.3.3", {"start": v(-78.51, -15.01) * mm, "end": v(-78.51, -10.39) * mm});
            skLineSegment(sketch, "E28.0.4.0", {"start": v(-78.51, -23.09) * mm, "end": v(-73.89, -23.09) * mm});
            skLineSegment(sketch, "E28.0.4.1", {"start": v(-73.89, -27.71) * mm, "end": v(-73.89, -23.09) * mm});
            skLineSegment(sketch, "E28.0.4.2", {"start": v(-78.51, -27.71) * mm, "end": v(-73.89, -27.71) * mm});
            skLineSegment(sketch, "E28.0.4.3", {"start": v(-78.51, -27.71) * mm, "end": v(-78.51, -23.09) * mm});
            skLineSegment(sketch, "E28.1.0.0", {"start": v(-65.81, 27.71) * mm, "end": v(-61.19, 27.71) * mm});
            skLineSegment(sketch, "E28.1.0.1", {"start": v(-61.19, 23.09) * mm, "end": v(-61.19, 27.71) * mm});
            skLineSegment(sketch, "E28.1.0.2", {"start": v(-65.81, 23.09) * mm, "end": v(-61.19, 23.09) * mm});
            skLineSegment(sketch, "E28.1.0.3", {"start": v(-65.81, 23.09) * mm, "end": v(-65.81, 27.71) * mm});
            skLineSegment(sketch, "E28.1.1.0", {"start": v(-65.81, 15.01) * mm, "end": v(-61.19, 15.01) * mm});
            skLineSegment(sketch, "E28.1.1.1", {"start": v(-61.19, 10.39) * mm, "end": v(-61.19, 15.01) * mm});
            skLineSegment(sketch, "E28.1.1.2", {"start": v(-65.81, 10.39) * mm, "end": v(-61.19, 10.39) * mm});
            skLineSegment(sketch, "E28.1.1.3", {"start": v(-65.81, 10.39) * mm, "end": v(-65.81, 15.01) * mm});
            skLineSegment(sketch, "E28.1.2.0", {"start": v(-65.81, 2.31) * mm, "end": v(-61.19, 2.31) * mm});
            skLineSegment(sketch, "E28.1.2.1", {"start": v(-61.19, -2.31) * mm, "end": v(-61.19, 2.31) * mm});
            skLineSegment(sketch, "E28.1.2.2", {"start": v(-65.81, -2.31) * mm, "end": v(-61.19, -2.31) * mm});
            skLineSegment(sketch, "E28.1.2.3", {"start": v(-65.81, -2.31) * mm, "end": v(-65.81, 2.31) * mm});
            skLineSegment(sketch, "E28.1.3.0", {"start": v(-65.81, -10.39) * mm, "end": v(-61.19, -10.39) * mm});
            skLineSegment(sketch, "E28.1.3.1", {"start": v(-61.19, -15.01) * mm, "end": v(-61.19, -10.39) * mm});
            skLineSegment(sketch, "E28.1.3.2", {"start": v(-65.81, -15.01) * mm, "end": v(-61.19, -15.01) * mm});
            skLineSegment(sketch, "E28.1.3.3", {"start": v(-65.81, -15.01) * mm, "end": v(-65.81, -10.39) * mm});
            skLineSegment(sketch, "E28.1.4.0", {"start": v(-65.81, -23.09) * mm, "end": v(-61.19, -23.09) * mm});
            skLineSegment(sketch, "E28.1.4.1", {"start": v(-61.19, -27.71) * mm, "end": v(-61.19, -23.09) * mm});
            skLineSegment(sketch, "E28.1.4.2", {"start": v(-65.81, -27.71) * mm, "end": v(-61.19, -27.71) * mm});
            skLineSegment(sketch, "E28.1.4.3", {"start": v(-65.81, -27.71) * mm, "end": v(-65.81, -23.09) * mm});
            skLineSegment(sketch, "E28.2.0.0", {"start": v(-53.11, 27.71) * mm, "end": v(-48.49, 27.71) * mm});
            skLineSegment(sketch, "E28.2.0.1", {"start": v(-48.49, 23.09) * mm, "end": v(-48.49, 27.71) * mm});
            skLineSegment(sketch, "E28.2.0.2", {"start": v(-53.11, 23.09) * mm, "end": v(-48.49, 23.09) * mm});
            skLineSegment(sketch, "E28.2.0.3", {"start": v(-53.11, 23.09) * mm, "end": v(-53.11, 27.71) * mm});
            skLineSegment(sketch, "E28.2.1.0", {"start": v(-53.11, 15.01) * mm, "end": v(-48.49, 15.01) * mm});
            skLineSegment(sketch, "E28.2.1.1", {"start": v(-48.49, 10.39) * mm, "end": v(-48.49, 15.01) * mm});
            skLineSegment(sketch, "E28.2.1.2", {"start": v(-53.11, 10.39) * mm, "end": v(-48.49, 10.39) * mm});
            skLineSegment(sketch, "E28.2.1.3", {"start": v(-53.11, 10.39) * mm, "end": v(-53.11, 15.01) * mm});
            skLineSegment(sketch, "E28.2.2.0", {"start": v(-53.11, 2.31) * mm, "end": v(-48.49, 2.31) * mm});
            skLineSegment(sketch, "E28.2.2.1", {"start": v(-48.49, -2.31) * mm, "end": v(-48.49, 2.31) * mm});
            skLineSegment(sketch, "E28.2.2.2", {"start": v(-53.11, -2.31) * mm, "end": v(-48.49, -2.31) * mm});
            skLineSegment(sketch, "E28.2.2.3", {"start": v(-53.11, -2.31) * mm, "end": v(-53.11, 2.31) * mm});
            skLineSegment(sketch, "E28.2.3.0", {"start": v(-53.11, -10.39) * mm, "end": v(-48.49, -10.39) * mm});
            skLineSegment(sketch, "E28.2.3.1", {"start": v(-48.49, -15.01) * mm, "end": v(-48.49, -10.39) * mm});
            skLineSegment(sketch, "E28.2.3.2", {"start": v(-53.11, -15.01) * mm, "end": v(-48.49, -15.01) * mm});
            skLineSegment(sketch, "E28.2.3.3", {"start": v(-53.11, -15.01) * mm, "end": v(-53.11, -10.39) * mm});
            skLineSegment(sketch, "E28.2.4.0", {"start": v(-53.11, -23.09) * mm, "end": v(-48.49, -23.09) * mm});
            skLineSegment(sketch, "E28.2.4.1", {"start": v(-48.49, -27.71) * mm, "end": v(-48.49, -23.09) * mm});
            skLineSegment(sketch, "E28.2.4.2", {"start": v(-53.11, -27.71) * mm, "end": v(-48.49, -27.71) * mm});
            skLineSegment(sketch, "E28.2.4.3", {"start": v(-53.11, -27.71) * mm, "end": v(-53.11, -23.09) * mm});
            skLineSegment(sketch, "E28.3.0.0", {"start": v(-40.41, 27.71) * mm, "end": v(-35.79, 27.71) * mm});
            skLineSegment(sketch, "E28.3.0.1", {"start": v(-35.79, 23.09) * mm, "end": v(-35.79, 27.71) * mm});
            skLineSegment(sketch, "E28.3.0.2", {"start": v(-40.41, 23.09) * mm, "end": v(-35.79, 23.09) * mm});
            skLineSegment(sketch, "E28.3.0.3", {"start": v(-40.41, 23.09) * mm, "end": v(-40.41, 27.71) * mm});
            skLineSegment(sketch, "E28.3.1.0", {"start": v(-40.41, 15.01) * mm, "end": v(-35.79, 15.01) * mm});
            skLineSegment(sketch, "E28.3.1.1", {"start": v(-35.79, 10.39) * mm, "end": v(-35.79, 15.01) * mm});
            skLineSegment(sketch, "E28.3.1.2", {"start": v(-40.41, 10.39) * mm, "end": v(-35.79, 10.39) * mm});
            skLineSegment(sketch, "E28.3.1.3", {"start": v(-40.41, 10.39) * mm, "end": v(-40.41, 15.01) * mm});
            skLineSegment(sketch, "E28.3.2.0", {"start": v(-40.41, 2.31) * mm, "end": v(-35.79, 2.31) * mm});
            skLineSegment(sketch, "E28.3.2.1", {"start": v(-35.79, -2.31) * mm, "end": v(-35.79, 2.31) * mm});
            skLineSegment(sketch, "E28.3.2.2", {"start": v(-40.41, -2.31) * mm, "end": v(-35.79, -2.31) * mm});
            skLineSegment(sketch, "E28.3.2.3", {"start": v(-40.41, -2.31) * mm, "end": v(-40.41, 2.31) * mm});
            skLineSegment(sketch, "E28.3.3.0", {"start": v(-40.41, -10.39) * mm, "end": v(-35.79, -10.39) * mm});
            skLineSegment(sketch, "E28.3.3.1", {"start": v(-35.79, -15.01) * mm, "end": v(-35.79, -10.39) * mm});
            skLineSegment(sketch, "E28.3.3.2", {"start": v(-40.41, -15.01) * mm, "end": v(-35.79, -15.01) * mm});
            skLineSegment(sketch, "E28.3.3.3", {"start": v(-40.41, -15.01) * mm, "end": v(-40.41, -10.39) * mm});
            skLineSegment(sketch, "E28.3.4.0", {"start": v(-40.41, -23.09) * mm, "end": v(-35.79, -23.09) * mm});
            skLineSegment(sketch, "E28.3.4.1", {"start": v(-35.79, -27.71) * mm, "end": v(-35.79, -23.09) * mm});
            skLineSegment(sketch, "E28.3.4.2", {"start": v(-40.41, -27.71) * mm, "end": v(-35.79, -27.71) * mm});
            skLineSegment(sketch, "E28.3.4.3", {"start": v(-40.41, -27.71) * mm, "end": v(-40.41, -23.09) * mm});
            skLineSegment(sketch, "E28.4.0.0", {"start": v(-27.71, 27.71) * mm, "end": v(-23.09, 27.71) * mm});
            skLineSegment(sketch, "E28.4.0.1", {"start": v(-23.09, 23.09) * mm, "end": v(-23.09, 27.71) * mm});
            skLineSegment(sketch, "E28.4.0.2", {"start": v(-27.71, 23.09) * mm, "end": v(-23.09, 23.09) * mm});
            skLineSegment(sketch, "E28.4.0.3", {"start": v(-27.71, 23.09) * mm, "end": v(-27.71, 27.71) * mm});
            skLineSegment(sketch, "E28.4.1.0", {"start": v(-27.71, 15.01) * mm, "end": v(-23.09, 15.01) * mm});
            skLineSegment(sketch, "E28.4.1.1", {"start": v(-23.09, 10.39) * mm, "end": v(-23.09, 15.01) * mm});
            skLineSegment(sketch, "E28.4.1.2", {"start": v(-27.71, 10.39) * mm, "end": v(-23.09, 10.39) * mm});
            skLineSegment(sketch, "E28.4.1.3", {"start": v(-27.71, 10.39) * mm, "end": v(-27.71, 15.01) * mm});
            skLineSegment(sketch, "E28.4.2.0", {"start": v(-27.71, 2.31) * mm, "end": v(-23.09, 2.31) * mm});
            skLineSegment(sketch, "E28.4.2.1", {"start": v(-23.09, -2.31) * mm, "end": v(-23.09, 2.31) * mm});
            skLineSegment(sketch, "E28.4.2.2", {"start": v(-27.71, -2.31) * mm, "end": v(-23.09, -2.31) * mm});
            skLineSegment(sketch, "E28.4.2.3", {"start": v(-27.71, -2.31) * mm, "end": v(-27.71, 2.31) * mm});
            skLineSegment(sketch, "E28.4.3.0", {"start": v(-27.71, -10.39) * mm, "end": v(-23.09, -10.39) * mm});
            skLineSegment(sketch, "E28.4.3.1", {"start": v(-23.09, -15.01) * mm, "end": v(-23.09, -10.39) * mm});
            skLineSegment(sketch, "E28.4.3.2", {"start": v(-27.71, -15.01) * mm, "end": v(-23.09, -15.01) * mm});
            skLineSegment(sketch, "E28.4.3.3", {"start": v(-27.71, -15.01) * mm, "end": v(-27.71, -10.39) * mm});
            skLineSegment(sketch, "E28.4.4.0", {"start": v(-27.71, -23.09) * mm, "end": v(-23.09, -23.09) * mm});
            skLineSegment(sketch, "E28.4.4.1", {"start": v(-23.09, -27.71) * mm, "end": v(-23.09, -23.09) * mm});
            skLineSegment(sketch, "E28.4.4.2", {"start": v(-27.71, -27.71) * mm, "end": v(-23.09, -27.71) * mm});
            skLineSegment(sketch, "E28.4.4.3", {"start": v(-27.71, -27.71) * mm, "end": v(-27.71, -23.09) * mm});
            skLineSegment(sketch, "E28.5.0.0", {"start": v(-15.01, 27.71) * mm, "end": v(-10.39, 27.71) * mm});
            skLineSegment(sketch, "E28.5.0.1", {"start": v(-10.39, 23.09) * mm, "end": v(-10.39, 27.71) * mm});
            skLineSegment(sketch, "E28.5.0.2", {"start": v(-15.01, 23.09) * mm, "end": v(-10.39, 23.09) * mm});
            skLineSegment(sketch, "E28.5.0.3", {"start": v(-15.01, 23.09) * mm, "end": v(-15.01, 27.71) * mm});
            skLineSegment(sketch, "E28.5.1.0", {"start": v(-15.01, 15.01) * mm, "end": v(-10.39, 15.01) * mm});
            skLineSegment(sketch, "E28.5.1.1", {"start": v(-10.39, 10.39) * mm, "end": v(-10.39, 15.01) * mm});
            skLineSegment(sketch, "E28.5.1.2", {"start": v(-15.01, 10.39) * mm, "end": v(-10.39, 10.39) * mm});
            skLineSegment(sketch, "E28.5.1.3", {"start": v(-15.01, 10.39) * mm, "end": v(-15.01, 15.01) * mm});
            skLineSegment(sketch, "E28.5.2.0", {"start": v(-15.01, 2.31) * mm, "end": v(-10.39, 2.31) * mm});
            skLineSegment(sketch, "E28.5.2.1", {"start": v(-10.39, -2.31) * mm, "end": v(-10.39, 2.31) * mm});
            skLineSegment(sketch, "E28.5.2.2", {"start": v(-15.01, -2.31) * mm, "end": v(-10.39, -2.31) * mm});
            skLineSegment(sketch, "E28.5.2.3", {"start": v(-15.01, -2.31) * mm, "end": v(-15.01, 2.31) * mm});
            skLineSegment(sketch, "E28.5.3.0", {"start": v(-15.01, -10.39) * mm, "end": v(-10.39, -10.39) * mm});
            skLineSegment(sketch, "E28.5.3.1", {"start": v(-10.39, -15.01) * mm, "end": v(-10.39, -10.39) * mm});
            skLineSegment(sketch, "E28.5.3.2", {"start": v(-15.01, -15.01) * mm, "end": v(-10.39, -15.01) * mm});
            skLineSegment(sketch, "E28.5.3.3", {"start": v(-15.01, -15.01) * mm, "end": v(-15.01, -10.39) * mm});
            skLineSegment(sketch, "E28.5.4.0", {"start": v(-15.01, -23.09) * mm, "end": v(-10.39, -23.09) * mm});
            skLineSegment(sketch, "E28.5.4.1", {"start": v(-10.39, -27.71) * mm, "end": v(-10.39, -23.09) * mm});
            skLineSegment(sketch, "E28.5.4.2", {"start": v(-15.01, -27.71) * mm, "end": v(-10.39, -27.71) * mm});
            skLineSegment(sketch, "E28.5.4.3", {"start": v(-15.01, -27.71) * mm, "end": v(-15.01, -23.09) * mm});
            skLineSegment(sketch, "E28.6.0.0", {"start": v(-2.31, 27.71) * mm, "end": v(2.31, 27.71) * mm});
            skLineSegment(sketch, "E28.6.0.1", {"start": v(2.31, 23.09) * mm, "end": v(2.31, 27.71) * mm});
            skLineSegment(sketch, "E28.6.0.2", {"start": v(-2.31, 23.09) * mm, "end": v(2.31, 23.09) * mm});
            skLineSegment(sketch, "E28.6.0.3", {"start": v(-2.31, 23.09) * mm, "end": v(-2.31, 27.71) * mm});
            skLineSegment(sketch, "E28.6.1.0", {"start": v(-2.31, 15.01) * mm, "end": v(2.31, 15.01) * mm});
            skLineSegment(sketch, "E28.6.1.1", {"start": v(2.31, 10.39) * mm, "end": v(2.31, 15.01) * mm});
            skLineSegment(sketch, "E28.6.1.2", {"start": v(-2.31, 10.39) * mm, "end": v(2.31, 10.39) * mm});
            skLineSegment(sketch, "E28.6.1.3", {"start": v(-2.31, 10.39) * mm, "end": v(-2.31, 15.01) * mm});
            skLineSegment(sketch, "E28.6.2.0", {"start": v(-2.31, 2.31) * mm, "end": v(2.31, 2.31) * mm});
            skLineSegment(sketch, "E28.6.2.1", {"start": v(2.31, -2.31) * mm, "end": v(2.31, 2.31) * mm});
            skLineSegment(sketch, "E28.6.2.2", {"start": v(-2.31, -2.31) * mm, "end": v(2.31, -2.31) * mm});
            skLineSegment(sketch, "E28.6.2.3", {"start": v(-2.31, -2.31) * mm, "end": v(-2.31, 2.31) * mm});
            skLineSegment(sketch, "E28.6.3.0", {"start": v(-2.31, -10.39) * mm, "end": v(2.31, -10.39) * mm});
            skLineSegment(sketch, "E28.6.3.1", {"start": v(2.31, -15.01) * mm, "end": v(2.31, -10.39) * mm});
            skLineSegment(sketch, "E28.6.3.2", {"start": v(-2.31, -15.01) * mm, "end": v(2.31, -15.01) * mm});
            skLineSegment(sketch, "E28.6.3.3", {"start": v(-2.31, -15.01) * mm, "end": v(-2.31, -10.39) * mm});
            skLineSegment(sketch, "E28.6.4.0", {"start": v(-2.31, -23.09) * mm, "end": v(2.31, -23.09) * mm});
            skLineSegment(sketch, "E28.6.4.1", {"start": v(2.31, -27.71) * mm, "end": v(2.31, -23.09) * mm});
            skLineSegment(sketch, "E28.6.4.2", {"start": v(-2.31, -27.71) * mm, "end": v(2.31, -27.71) * mm});
            skLineSegment(sketch, "E28.6.4.3", {"start": v(-2.31, -27.71) * mm, "end": v(-2.31, -23.09) * mm});
            skLineSegment(sketch, "E28.7.0.0", {"start": v(10.39, 27.71) * mm, "end": v(15.01, 27.71) * mm});
            skLineSegment(sketch, "E28.7.0.1", {"start": v(15.01, 23.09) * mm, "end": v(15.01, 27.71) * mm});
            skLineSegment(sketch, "E28.7.0.2", {"start": v(10.39, 23.09) * mm, "end": v(15.01, 23.09) * mm});
            skLineSegment(sketch, "E28.7.0.3", {"start": v(10.39, 23.09) * mm, "end": v(10.39, 27.71) * mm});
            skLineSegment(sketch, "E28.7.1.0", {"start": v(10.39, 15.01) * mm, "end": v(15.01, 15.01) * mm});
            skLineSegment(sketch, "E28.7.1.1", {"start": v(15.01, 10.39) * mm, "end": v(15.01, 15.01) * mm});
            skLineSegment(sketch, "E28.7.1.2", {"start": v(10.39, 10.39) * mm, "end": v(15.01, 10.39) * mm});
            skLineSegment(sketch, "E28.7.1.3", {"start": v(10.39, 10.39) * mm, "end": v(10.39, 15.01) * mm});
            skLineSegment(sketch, "E28.7.2.0", {"start": v(10.39, 2.31) * mm, "end": v(15.01, 2.31) * mm});
            skLineSegment(sketch, "E28.7.2.1", {"start": v(15.01, -2.31) * mm, "end": v(15.01, 2.31) * mm});
            skLineSegment(sketch, "E28.7.2.2", {"start": v(10.39, -2.31) * mm, "end": v(15.01, -2.31) * mm});
            skLineSegment(sketch, "E28.7.2.3", {"start": v(10.39, -2.31) * mm, "end": v(10.39, 2.31) * mm});
            skLineSegment(sketch, "E28.7.3.0", {"start": v(10.39, -10.39) * mm, "end": v(15.01, -10.39) * mm});
            skLineSegment(sketch, "E28.7.3.1", {"start": v(15.01, -15.01) * mm, "end": v(15.01, -10.39) * mm});
            skLineSegment(sketch, "E28.7.3.2", {"start": v(10.39, -15.01) * mm, "end": v(15.01, -15.01) * mm});
            skLineSegment(sketch, "E28.7.3.3", {"start": v(10.39, -15.01) * mm, "end": v(10.39, -10.39) * mm});
            skLineSegment(sketch, "E28.7.4.0", {"start": v(10.39, -23.09) * mm, "end": v(15.01, -23.09) * mm});
            skLineSegment(sketch, "E28.7.4.1", {"start": v(15.01, -27.71) * mm, "end": v(15.01, -23.09) * mm});
            skLineSegment(sketch, "E28.7.4.2", {"start": v(10.39, -27.71) * mm, "end": v(15.01, -27.71) * mm});
            skLineSegment(sketch, "E28.7.4.3", {"start": v(10.39, -27.71) * mm, "end": v(10.39, -23.09) * mm});
            skLineSegment(sketch, "E28.8.0.0", {"start": v(23.09, 27.71) * mm, "end": v(27.71, 27.71) * mm});
            skLineSegment(sketch, "E28.8.0.1", {"start": v(27.71, 23.09) * mm, "end": v(27.71, 27.71) * mm});
            skLineSegment(sketch, "E28.8.0.2", {"start": v(23.09, 23.09) * mm, "end": v(27.71, 23.09) * mm});
            skLineSegment(sketch, "E28.8.0.3", {"start": v(23.09, 23.09) * mm, "end": v(23.09, 27.71) * mm});
            skLineSegment(sketch, "E28.8.1.0", {"start": v(23.09, 15.01) * mm, "end": v(27.71, 15.01) * mm});
            skLineSegment(sketch, "E28.8.1.1", {"start": v(27.71, 10.39) * mm, "end": v(27.71, 15.01) * mm});
            skLineSegment(sketch, "E28.8.1.2", {"start": v(23.09, 10.39) * mm, "end": v(27.71, 10.39) * mm});
            skLineSegment(sketch, "E28.8.1.3", {"start": v(23.09, 10.39) * mm, "end": v(23.09, 15.01) * mm});
            skLineSegment(sketch, "E28.8.2.0", {"start": v(23.09, 2.31) * mm, "end": v(27.71, 2.31) * mm});
            skLineSegment(sketch, "E28.8.2.1", {"start": v(27.71, -2.31) * mm, "end": v(27.71, 2.31) * mm});
            skLineSegment(sketch, "E28.8.2.2", {"start": v(23.09, -2.31) * mm, "end": v(27.71, -2.31) * mm});
            skLineSegment(sketch, "E28.8.2.3", {"start": v(23.09, -2.31) * mm, "end": v(23.09, 2.31) * mm});
            skLineSegment(sketch, "E28.8.3.0", {"start": v(23.09, -10.39) * mm, "end": v(27.71, -10.39) * mm});
            skLineSegment(sketch, "E28.8.3.1", {"start": v(27.71, -15.01) * mm, "end": v(27.71, -10.39) * mm});
            skLineSegment(sketch, "E28.8.3.2", {"start": v(23.09, -15.01) * mm, "end": v(27.71, -15.01) * mm});
            skLineSegment(sketch, "E28.8.3.3", {"start": v(23.09, -15.01) * mm, "end": v(23.09, -10.39) * mm});
            skLineSegment(sketch, "E28.8.4.0", {"start": v(23.09, -23.09) * mm, "end": v(27.71, -23.09) * mm});
            skLineSegment(sketch, "E28.8.4.1", {"start": v(27.71, -27.71) * mm, "end": v(27.71, -23.09) * mm});
            skLineSegment(sketch, "E28.8.4.2", {"start": v(23.09, -27.71) * mm, "end": v(27.71, -27.71) * mm});
            skLineSegment(sketch, "E28.8.4.3", {"start": v(23.09, -27.71) * mm, "end": v(23.09, -23.09) * mm});
            skLineSegment(sketch, "E28.9.0.0", {"start": v(35.79, 27.71) * mm, "end": v(40.41, 27.71) * mm});
            skLineSegment(sketch, "E28.9.0.1", {"start": v(40.41, 23.09) * mm, "end": v(40.41, 27.71) * mm});
            skLineSegment(sketch, "E28.9.0.2", {"start": v(35.79, 23.09) * mm, "end": v(40.41, 23.09) * mm});
            skLineSegment(sketch, "E28.9.0.3", {"start": v(35.79, 23.09) * mm, "end": v(35.79, 27.71) * mm});
            skLineSegment(sketch, "E28.9.1.0", {"start": v(35.79, 15.01) * mm, "end": v(40.41, 15.01) * mm});
            skLineSegment(sketch, "E28.9.1.1", {"start": v(40.41, 10.39) * mm, "end": v(40.41, 15.01) * mm});
            skLineSegment(sketch, "E28.9.1.2", {"start": v(35.79, 10.39) * mm, "end": v(40.41, 10.39) * mm});
            skLineSegment(sketch, "E28.9.1.3", {"start": v(35.79, 10.39) * mm, "end": v(35.79, 15.01) * mm});
            skLineSegment(sketch, "E28.9.2.0", {"start": v(35.79, 2.31) * mm, "end": v(40.41, 2.31) * mm});
            skLineSegment(sketch, "E28.9.2.1", {"start": v(40.41, -2.31) * mm, "end": v(40.41, 2.31) * mm});
            skLineSegment(sketch, "E28.9.2.2", {"start": v(35.79, -2.31) * mm, "end": v(40.41, -2.31) * mm});
            skLineSegment(sketch, "E28.9.2.3", {"start": v(35.79, -2.31) * mm, "end": v(35.79, 2.31) * mm});
            skLineSegment(sketch, "E28.9.3.0", {"start": v(35.79, -10.39) * mm, "end": v(40.41, -10.39) * mm});
            skLineSegment(sketch, "E28.9.3.1", {"start": v(40.41, -15.01) * mm, "end": v(40.41, -10.39) * mm});
            skLineSegment(sketch, "E28.9.3.2", {"start": v(35.79, -15.01) * mm, "end": v(40.41, -15.01) * mm});
            skLineSegment(sketch, "E28.9.3.3", {"start": v(35.79, -15.01) * mm, "end": v(35.79, -10.39) * mm});
            skLineSegment(sketch, "E28.9.4.0", {"start": v(35.79, -23.09) * mm, "end": v(40.41, -23.09) * mm});
            skLineSegment(sketch, "E28.9.4.1", {"start": v(40.41, -27.71) * mm, "end": v(40.41, -23.09) * mm});
            skLineSegment(sketch, "E28.9.4.2", {"start": v(35.79, -27.71) * mm, "end": v(40.41, -27.71) * mm});
            skLineSegment(sketch, "E28.9.4.3", {"start": v(35.79, -27.71) * mm, "end": v(35.79, -23.09) * mm});
            skLineSegment(sketch, "E28.10.0.0", {"start": v(48.49, 27.71) * mm, "end": v(53.11, 27.71) * mm});
            skLineSegment(sketch, "E28.10.0.1", {"start": v(53.11, 23.09) * mm, "end": v(53.11, 27.71) * mm});
            skLineSegment(sketch, "E28.10.0.2", {"start": v(48.49, 23.09) * mm, "end": v(53.11, 23.09) * mm});
            skLineSegment(sketch, "E28.10.0.3", {"start": v(48.49, 23.09) * mm, "end": v(48.49, 27.71) * mm});
            skLineSegment(sketch, "E28.10.1.0", {"start": v(48.49, 15.01) * mm, "end": v(53.11, 15.01) * mm});
            skLineSegment(sketch, "E28.10.1.1", {"start": v(53.11, 10.39) * mm, "end": v(53.11, 15.01) * mm});
            skLineSegment(sketch, "E28.10.1.2", {"start": v(48.49, 10.39) * mm, "end": v(53.11, 10.39) * mm});
            skLineSegment(sketch, "E28.10.1.3", {"start": v(48.49, 10.39) * mm, "end": v(48.49, 15.01) * mm});
            skLineSegment(sketch, "E28.10.2.0", {"start": v(48.49, 2.31) * mm, "end": v(53.11, 2.31) * mm});
            skLineSegment(sketch, "E28.10.2.1", {"start": v(53.11, -2.31) * mm, "end": v(53.11, 2.31) * mm});
            skLineSegment(sketch, "E28.10.2.2", {"start": v(48.49, -2.31) * mm, "end": v(53.11, -2.31) * mm});
            skLineSegment(sketch, "E28.10.2.3", {"start": v(48.49, -2.31) * mm, "end": v(48.49, 2.31) * mm});
            skLineSegment(sketch, "E28.10.3.0", {"start": v(48.49, -10.39) * mm, "end": v(53.11, -10.39) * mm});
            skLineSegment(sketch, "E28.10.3.1", {"start": v(53.11, -15.01) * mm, "end": v(53.11, -10.39) * mm});
            skLineSegment(sketch, "E28.10.3.2", {"start": v(48.49, -15.01) * mm, "end": v(53.11, -15.01) * mm});
            skLineSegment(sketch, "E28.10.3.3", {"start": v(48.49, -15.01) * mm, "end": v(48.49, -10.39) * mm});
            skLineSegment(sketch, "E28.10.4.0", {"start": v(48.49, -23.09) * mm, "end": v(53.11, -23.09) * mm});
            skLineSegment(sketch, "E28.10.4.1", {"start": v(53.11, -27.71) * mm, "end": v(53.11, -23.09) * mm});
            skLineSegment(sketch, "E28.10.4.2", {"start": v(48.49, -27.71) * mm, "end": v(53.11, -27.71) * mm});
            skLineSegment(sketch, "E28.10.4.3", {"start": v(48.49, -27.71) * mm, "end": v(48.49, -23.09) * mm});
            skLineSegment(sketch, "E28.11.0.0", {"start": v(61.19, 27.71) * mm, "end": v(65.81, 27.71) * mm});
            skLineSegment(sketch, "E28.11.0.1", {"start": v(65.81, 23.09) * mm, "end": v(65.81, 27.71) * mm});
            skLineSegment(sketch, "E28.11.0.2", {"start": v(61.19, 23.09) * mm, "end": v(65.81, 23.09) * mm});
            skLineSegment(sketch, "E28.11.0.3", {"start": v(61.19, 23.09) * mm, "end": v(61.19, 27.71) * mm});
            skLineSegment(sketch, "E28.11.1.0", {"start": v(61.19, 15.01) * mm, "end": v(65.81, 15.01) * mm});
            skLineSegment(sketch, "E28.11.1.1", {"start": v(65.81, 10.39) * mm, "end": v(65.81, 15.01) * mm});
            skLineSegment(sketch, "E28.11.1.2", {"start": v(61.19, 10.39) * mm, "end": v(65.81, 10.39) * mm});
            skLineSegment(sketch, "E28.11.1.3", {"start": v(61.19, 10.39) * mm, "end": v(61.19, 15.01) * mm});
            skLineSegment(sketch, "E28.11.2.0", {"start": v(61.19, 2.31) * mm, "end": v(65.81, 2.31) * mm});
            skLineSegment(sketch, "E28.11.2.1", {"start": v(65.81, -2.31) * mm, "end": v(65.81, 2.31) * mm});
            skLineSegment(sketch, "E28.11.2.2", {"start": v(61.19, -2.31) * mm, "end": v(65.81, -2.31) * mm});
            skLineSegment(sketch, "E28.11.2.3", {"start": v(61.19, -2.31) * mm, "end": v(61.19, 2.31) * mm});
            skLineSegment(sketch, "E28.11.3.0", {"start": v(61.19, -10.39) * mm, "end": v(65.81, -10.39) * mm});
            skLineSegment(sketch, "E28.11.3.1", {"start": v(65.81, -15.01) * mm, "end": v(65.81, -10.39) * mm});
            skLineSegment(sketch, "E28.11.3.2", {"start": v(61.19, -15.01) * mm, "end": v(65.81, -15.01) * mm});
            skLineSegment(sketch, "E28.11.3.3", {"start": v(61.19, -15.01) * mm, "end": v(61.19, -10.39) * mm});
            skLineSegment(sketch, "E28.11.4.0", {"start": v(61.19, -23.09) * mm, "end": v(65.81, -23.09) * mm});
            skLineSegment(sketch, "E28.11.4.1", {"start": v(65.81, -27.71) * mm, "end": v(65.81, -23.09) * mm});
            skLineSegment(sketch, "E28.11.4.2", {"start": v(61.19, -27.71) * mm, "end": v(65.81, -27.71) * mm});
            skLineSegment(sketch, "E28.11.4.3", {"start": v(61.19, -27.71) * mm, "end": v(61.19, -23.09) * mm});
            skLineSegment(sketch, "E28.12.0.0", {"start": v(73.89, 27.71) * mm, "end": v(78.51, 27.71) * mm});
            skLineSegment(sketch, "E28.12.0.1", {"start": v(78.51, 23.09) * mm, "end": v(78.51, 27.71) * mm});
            skLineSegment(sketch, "E28.12.0.2", {"start": v(73.89, 23.09) * mm, "end": v(78.51, 23.09) * mm});
            skLineSegment(sketch, "E28.12.0.3", {"start": v(73.89, 23.09) * mm, "end": v(73.89, 27.71) * mm});
            skLineSegment(sketch, "E28.12.1.0", {"start": v(73.89, 15.01) * mm, "end": v(78.51, 15.01) * mm});
            skLineSegment(sketch, "E28.12.1.1", {"start": v(78.51, 10.39) * mm, "end": v(78.51, 15.01) * mm});
            skLineSegment(sketch, "E28.12.1.2", {"start": v(73.89, 10.39) * mm, "end": v(78.51, 10.39) * mm});
            skLineSegment(sketch, "E28.12.1.3", {"start": v(73.89, 10.39) * mm, "end": v(73.89, 15.01) * mm});
            skLineSegment(sketch, "E28.12.2.0", {"start": v(73.89, 2.31) * mm, "end": v(78.51, 2.31) * mm});
            skLineSegment(sketch, "E28.12.2.1", {"start": v(78.51, -2.31) * mm, "end": v(78.51, 2.31) * mm});
            skLineSegment(sketch, "E28.12.2.2", {"start": v(73.89, -2.31) * mm, "end": v(78.51, -2.31) * mm});
            skLineSegment(sketch, "E28.12.2.3", {"start": v(73.89, -2.31) * mm, "end": v(73.89, 2.31) * mm});
            skLineSegment(sketch, "E28.12.3.0", {"start": v(73.89, -10.39) * mm, "end": v(78.51, -10.39) * mm});
            skLineSegment(sketch, "E28.12.3.1", {"start": v(78.51, -15.01) * mm, "end": v(78.51, -10.39) * mm});
            skLineSegment(sketch, "E28.12.3.2", {"start": v(73.89, -15.01) * mm, "end": v(78.51, -15.01) * mm});
            skLineSegment(sketch, "E28.12.3.3", {"start": v(73.89, -15.01) * mm, "end": v(73.89, -10.39) * mm});
            skLineSegment(sketch, "E28.12.4.0", {"start": v(73.89, -23.09) * mm, "end": v(78.51, -23.09) * mm});
            skLineSegment(sketch, "E28.12.4.1", {"start": v(78.51, -27.71) * mm, "end": v(78.51, -23.09) * mm});
            skLineSegment(sketch, "E28.12.4.2", {"start": v(73.89, -27.71) * mm, "end": v(78.51, -27.71) * mm});
            skLineSegment(sketch, "E28.12.4.3", {"start": v(73.89, -27.71) * mm, "end": v(73.89, -23.09) * mm});
            skLineSegment(sketch, "E28.direction1", {"start": v(-78.51, 27.71) * mm, "end": v(-65.81, 27.71) * mm, "construction": true});
            skLineSegment(sketch, "E28.direction2", {"start": v(-78.51, 27.71) * mm, "end": v(-78.51, 15.01) * mm, "construction": true});
            skLineSegment(sketch, "E29", {"start": v(-65.36, -38.1) * mm, "end": v(-65.36, -34.93) * mm});
            skSolve(sketch);
        }
        {
            var Q0;
            Q0=makeQuery(id+"F0.imprint","IMPRINT",FACE,{"disambiguationData":[TD([[makeQuery(id+"F0.imprint","IMPRINT",EDGE,{"derivedFrom":sQuery(id+"F0.wireOp",EDGE,"E0.rect.bottom")}),1.0]])]});
            extrude(context, id + "F1", {"entities" : qUnion([Q0]), "depth" : 3.17 * mm});
        }
    });
